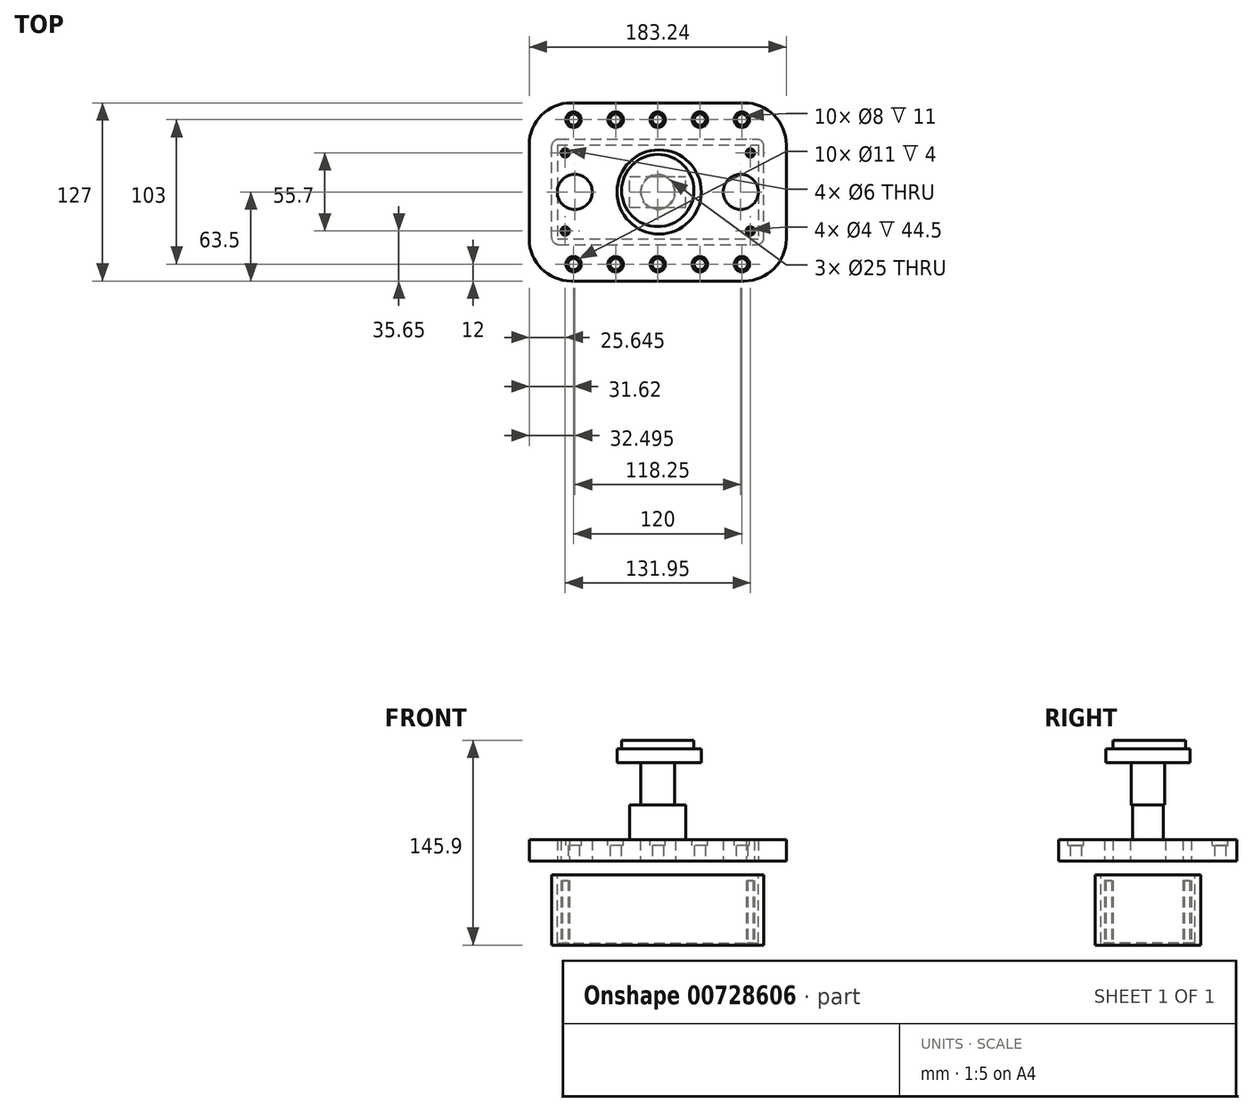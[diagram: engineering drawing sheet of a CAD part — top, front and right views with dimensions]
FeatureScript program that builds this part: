
annotation { "Feature Type Name" : "Feature", "Feature Type Description" : "" }
export const myFeature = defineFeature(function(context is Context, id is Id, definition is map)
    precondition{}
    {
        {
            var Q0;
            Q0=qCreatedBy(makeId("Top.planeOp"),FACE);
            var sketch = newSketch(context, id + "F0", { "sketchPlane" : qUnion([Q0])});
            skCircle(sketch, "E0", {"center": v(0, 1.03) * mm, "radius": 25.75 * mm});
            skSolve(sketch);
        }
        {
            var Q0;
            Q0 = qSketchRegion(id + "F0", true);
            extrude(context, id + "F1", {"entities" : qUnion([Q0]), "depth" : 5.9 * mm, "offsetDistance" : 25 * mm});
        }
        {
            var Q0;
            Q0=makeQuery(id+"F1.opExtrude","CAP_FACE",FACE,{"disambiguationData":[OSD([sQuery(id+"F0.wireOp",EDGE,"E0")])],"isStart":true});
            var sketch = newSketch(context, id + "F2", { "sketchPlane" : qUnion([Q0])});
            skCircle(sketch, "E1", {"center": v(1.03, 0) * mm, "radius": 30 * mm});
            skSolve(sketch);
        }
        {
            var Q0;
            Q0 = qSketchRegion(id + "F2", true);
            extrude(context, id + "F3", {"entities" : qUnion([Q0]), "operationType" : NewBodyOperationType.ADD, "depth" : 10.1 * mm, "offsetDistance" : 25 * mm});
        }
        {
            var Q0;
            Q0=makeQuery(id+"F3.opExtrude","CAP_FACE",FACE,{"disambiguationData":[OSD([sQuery(id+"F2.wireOp",EDGE,"E1")])],"isStart":false});
            var sketch = newSketch(context, id + "F4", { "sketchPlane" : qUnion([Q0])});
            skCircle(sketch, "E2", {"center": v(0, 0) * mm, "radius": 12 * mm});
            skSolve(sketch);
        }
        {
            var Q0;
            Q0 = qSketchRegion(id + "F4", true);
            extrude(context, id + "F5", {"entities" : qUnion([Q0]), "operationType" : NewBodyOperationType.ADD, "depth" : 30 * mm, "offsetDistance" : 25 * mm});
        }
        {
            var Q0;
            Q0=makeQuery(id+"F5.opExtrude","CAP_FACE",FACE,{"disambiguationData":[OSD([sQuery(id+"F4.wireOp",EDGE,"E2")])],"isStart":false});
            var sketch = newSketch(context, id + "F6", { "sketchPlane" : qUnion([Q0])});
            skLineSegment(sketch, "E3.bottom", {"start": v(-20, 11) * mm, "end": v(20, 11) * mm});
            skLineSegment(sketch, "E3.top", {"start": v(-20, -11) * mm, "end": v(20, -11) * mm});
            skLineSegment(sketch, "E3.left", {"start": v(-20, 11) * mm, "end": v(-20, -11) * mm});
            skLineSegment(sketch, "E3.right", {"start": v(20, 11) * mm, "end": v(20, -11) * mm});
            skPoint(sketch, "E3.middle", {"position": v(0, 0) * mm});
            skSolve(sketch);
        }
        {
            var Q0;
            Q0 = qSketchRegion(id + "F6", true);
            extrude(context, id + "F7", {"entities" : qUnion([Q0]), "operationType" : NewBodyOperationType.ADD, "depth" : 25 * mm, "offsetDistance" : 25 * mm});
        }
        {
            var Q0;
            Q0=qCreatedBy(makeId("Top.planeOp"),FACE);
            cPlane(context, id + "F8", {"entities" : qUnion([Q0]), "cplaneType" : CPlaneType.OFFSET, "offset" : 90 * mm, "oppositeDirection" : true, "width" : 150 * mm, "height" : 150 * mm});
        }
        {
            var Q0;
            Q0=qCreatedBy(id+"F8.planeOp",FACE);
            var sketch = newSketch(context, id + "F9", { "sketchPlane" : qUnion([Q0])});
            skLineSegment(sketch, "E4.bottom", {"start": v(-75.62, -37.5) * mm, "end": v(75.62, -37.5) * mm});
            skLineSegment(sketch, "E4.top", {"start": v(-75.62, 37.5) * mm, "end": v(75.62, 37.5) * mm});
            skLineSegment(sketch, "E4.left", {"start": v(-75.62, -37.5) * mm, "end": v(-75.62, 37.5) * mm});
            skLineSegment(sketch, "E4.right", {"start": v(75.62, -37.5) * mm, "end": v(75.62, 37.5) * mm});
            skPoint(sketch, "E4.middle", {"position": v(0, 0) * mm});
            skLineSegment(sketch, "E5.bottom", {"start": v(-71.62, 33.5) * mm, "end": v(71.62, 33.5) * mm});
            skLineSegment(sketch, "E5.top", {"start": v(-71.62, -33.5) * mm, "end": v(71.62, -33.5) * mm});
            skLineSegment(sketch, "E5.left", {"start": v(-71.62, 33.5) * mm, "end": v(-71.62, -33.5) * mm});
            skLineSegment(sketch, "E5.right", {"start": v(71.62, 33.5) * mm, "end": v(71.62, -33.5) * mm});
            skSolve(sketch);
        }
        {
            var Q0;
            Q0 = qSketchRegion(id + "F9", true);
            extrude(context, id + "F10", {"entities" : qUnion([Q0]), "oppositeDirection" : true, "depth" : 48.5 * mm, "offsetDistance" : 25 * mm});
        }
        {
            var Q0;
            Q0=makeQuery(id+"F10.opExtrude","CAP_FACE",FACE,{"disambiguationData":[OSD([sQuery(id+"F9.wireOp",EDGE,"E4.bottom"),sQuery(id+"F9.wireOp",EDGE,"E4.top"),sQuery(id+"F9.wireOp",EDGE,"E4.left"),sQuery(id+"F9.wireOp",EDGE,"E4.right"),sQuery(id+"F9.wireOp",EDGE,"E5.bottom"),sQuery(id+"F9.wireOp",EDGE,"E5.top"),sQuery(id+"F9.wireOp",EDGE,"E5.left"),sQuery(id+"F9.wireOp",EDGE,"E5.right")])],"isStart":false});
            var sketch = newSketch(context, id + "F11", { "sketchPlane" : qUnion([Q0])});
            skLineSegment(sketch, "E6.bottom", {"start": v(-75.62, 37.5) * mm, "end": v(75.62, 37.5) * mm});
            skLineSegment(sketch, "E6.top", {"start": v(-75.62, -37.5) * mm, "end": v(75.62, -37.5) * mm});
            skLineSegment(sketch, "E6.left", {"start": v(-75.62, 37.5) * mm, "end": v(-75.62, -37.5) * mm});
            skLineSegment(sketch, "E6.right", {"start": v(75.62, 37.5) * mm, "end": v(75.62, -37.5) * mm});
            skSolve(sketch);
        }
        {
            var Q0;
            Q0 = qSketchRegion(id + "F11", true);
            extrude(context, id + "F12", {"entities" : qUnion([Q0]), "operationType" : NewBodyOperationType.ADD, "depth" : 1.5 * mm, "offsetDistance" : 25 * mm});
        }
        {
            var Q0;
            Q0=makeQuery(id+"F12.opExtrude","CAP_FACE",FACE,{"disambiguationData":[OSD([sQuery(id+"F11.wireOp",EDGE,"E6.bottom"),sQuery(id+"F11.wireOp",EDGE,"E6.top"),sQuery(id+"F11.wireOp",EDGE,"E6.left"),sQuery(id+"F11.wireOp",EDGE,"E6.right")])],"isStart":true});
            var sketch = newSketch(context, id + "F13", { "sketchPlane" : qUnion([Q0])});
            skCircle(sketch, "E7", {"center": v(65.97, 27.85) * mm, "radius": 3 * mm});
            skLineSegment(sketch, "E8", {"start": v(62.97, 33.5) * mm, "end": v(62.97, -33.5) * mm, "construction": true});
            skLineSegment(sketch, "E9", {"start": v(71.62, 24.85) * mm, "end": v(-71.62, 24.85) * mm, "construction": true});
            skCircle(sketch, "E10", {"center": v(65.97, 27.85) * mm, "radius": 2 * mm});
            skLineSegment(sketch, "E11", {"start": v(0, 33.5) * mm, "end": v(0, -33.5) * mm, "construction": true});
            skLineSegment(sketch, "E12", {"start": v(71.62, 0) * mm, "end": v(-71.62, 0) * mm, "construction": true});
            skCircle(sketch, "E13.MirrorC", {"center": v(-65.97, 27.85) * mm, "radius": 2 * mm});
            skCircle(sketch, "E14.MirrorC", {"center": v(-65.97, 27.85) * mm, "radius": 3 * mm});
            skCircle(sketch, "E15.MirrorC", {"center": v(65.97, -27.85) * mm, "radius": 2 * mm});
            skCircle(sketch, "E16.MirrorC", {"center": v(65.97, -27.85) * mm, "radius": 3 * mm});
            skCircle(sketch, "E17.MirrorC", {"center": v(-65.97, -27.85) * mm, "radius": 2 * mm});
            skCircle(sketch, "E18.MirrorC", {"center": v(-65.97, -27.85) * mm, "radius": 3 * mm});
            skSolve(sketch);
        }
        {
            var Q0;
            Q0 = qSketchRegion(id + "F13", true);
            extrude(context, id + "F14", {"entities" : qUnion([Q0]), "operationType" : NewBodyOperationType.ADD, "depth" : 44.5 * mm, "offsetDistance" : 25 * mm});
        }
        {
            var Q0;
            Q0=makeQuery(id+"F12.boolean.opBoolean","MERGE",EDGE,{"derivedFrom":[makeQuery(id+"F10.opExtrude","SWEPT_EDGE",EDGE,{"disambiguationData":[OSD([sQuery(id+"F9.wireOp",EDGE,"E4.top"),sQuery(id+"F9.wireOp",EDGE,"E4.left")])]}),makeQuery(id+"F12.opExtrude","SWEPT_EDGE",EDGE,{"disambiguationData":[OSD([sQuery(id+"F11.wireOp",EDGE,"E6.top"),sQuery(id+"F11.wireOp",EDGE,"E6.left")])]})]});
            var Q1;
            Q1=makeQuery(id+"F12.boolean.opBoolean","MERGE",EDGE,{"derivedFrom":[makeQuery(id+"F10.opExtrude","SWEPT_EDGE",EDGE,{"disambiguationData":[OSD([sQuery(id+"F9.wireOp",EDGE,"E4.bottom"),sQuery(id+"F9.wireOp",EDGE,"E4.left")])]}),makeQuery(id+"F12.opExtrude","SWEPT_EDGE",EDGE,{"disambiguationData":[OSD([sQuery(id+"F11.wireOp",EDGE,"E6.bottom"),sQuery(id+"F11.wireOp",EDGE,"E6.left")])]})]});
            var Q2;
            Q2=makeQuery(id+"F12.boolean.opBoolean","MERGE",EDGE,{"derivedFrom":[makeQuery(id+"F10.opExtrude","SWEPT_EDGE",EDGE,{"disambiguationData":[OSD([sQuery(id+"F9.wireOp",EDGE,"E4.bottom"),sQuery(id+"F9.wireOp",EDGE,"E4.right")])]}),makeQuery(id+"F12.opExtrude","SWEPT_EDGE",EDGE,{"disambiguationData":[OSD([sQuery(id+"F11.wireOp",EDGE,"E6.bottom"),sQuery(id+"F11.wireOp",EDGE,"E6.right")])]})]});
            var Q3;
            Q3=makeQuery(id+"F12.boolean.opBoolean","MERGE",EDGE,{"derivedFrom":[makeQuery(id+"F10.opExtrude","SWEPT_EDGE",EDGE,{"disambiguationData":[OSD([sQuery(id+"F9.wireOp",EDGE,"E4.top"),sQuery(id+"F9.wireOp",EDGE,"E4.right")])]}),makeQuery(id+"F12.opExtrude","SWEPT_EDGE",EDGE,{"disambiguationData":[OSD([sQuery(id+"F11.wireOp",EDGE,"E6.top"),sQuery(id+"F11.wireOp",EDGE,"E6.right")])]})]});
            fillet(context, id + "F15", {"entities" : qUnion([Q0, Q1, Q2, Q3]), "radius" : 5 * mm, "tangentPropagation" : true, "allowEdgeOverflow" : false});
        }
        {
            var Q0;
            Q0=qCreatedBy(id+"F8.planeOp",FACE);
            cPlane(context, id + "F16", {"entities" : qUnion([Q0]), "cplaneType" : CPlaneType.OFFSET, "offset" : 10 * mm, "width" : 150 * mm, "height" : 150 * mm});
        }
        {
            var Q0;
            Q0=qCreatedBy(id+"F16.planeOp",FACE);
            var sketch = newSketch(context, id + "F17", { "sketchPlane" : qUnion([Q0])});
            skLineSegment(sketch, "E19.0", {"start": v(-71.62, -33.5) * mm, "end": v(71.62, -33.5) * mm, "construction": true});
            skLineSegment(sketch, "E19.1", {"start": v(71.62, 33.5) * mm, "end": v(71.62, -33.5) * mm, "construction": true});
            skLineSegment(sketch, "E19.2", {"start": v(-71.62, 33.5) * mm, "end": v(71.62, 33.5) * mm, "construction": true});
            skLineSegment(sketch, "E19.3", {"start": v(-71.62, 33.5) * mm, "end": v(-71.62, -33.5) * mm, "construction": true});
            skLineSegment(sketch, "E20", {"start": v(71.62, 0) * mm, "end": v(-71.62, 0) * mm, "construction": true});
            skCircle(sketch, "E21", {"center": v(59.12, 0) * mm, "radius": 12.5 * mm});
            skCircle(sketch, "E22", {"center": v(59.12, 0) * mm, "radius": 30 * mm, "construction": true});
            skCircle(sketch, "E23", {"center": v(-59.12, 0) * mm, "radius": 12.5 * mm});
            skLineSegment(sketch, "E24", {"start": v(0, 33.5) * mm, "end": v(0, -33.5) * mm, "construction": true});
            skCircle(sketch, "E25", {"center": v(0, 0) * mm, "radius": 12.5 * mm});
            skCircle(sketch, "E26", {"center": v(0, 0) * mm, "radius": 30 * mm, "construction": true});
            skCircle(sketch, "E27", {"center": v(-59.12, 0) * mm, "radius": 30 * mm, "construction": true});
            skLineSegment(sketch, "E28.bottom", {"start": v(-91.62, 63.5) * mm, "end": v(91.62, 63.5) * mm});
            skLineSegment(sketch, "E28.top", {"start": v(-91.62, -63.5) * mm, "end": v(91.63, -63.5) * mm});
            skLineSegment(sketch, "E28.left", {"start": v(-91.62, 63.5) * mm, "end": v(-91.62, -63.5) * mm});
            skLineSegment(sketch, "E28.right", {"start": v(91.62, 63.5) * mm, "end": v(91.62, -63.5) * mm});
            skCircle(sketch, "E29.0", {"center": v(-65.97, -27.85) * mm, "radius": 3 * mm});
            skCircle(sketch, "E29.1", {"center": v(65.97, -27.85) * mm, "radius": 3 * mm});
            skCircle(sketch, "E29.2", {"center": v(65.97, 27.85) * mm, "radius": 3 * mm});
            skCircle(sketch, "E29.3", {"center": v(-65.97, 27.85) * mm, "radius": 3 * mm});
            skLineSegment(sketch, "E30", {"start": v(0, -33.5) * mm, "end": v(0, -63.5) * mm, "construction": true});
            skCircle(sketch, "E31", {"center": v(0, -51.5) * mm, "radius": 4 * mm});
            skCircle(sketch, "E32.1.0.0", {"center": v(30, -51.5) * mm, "radius": 4 * mm});
            skCircle(sketch, "E32.2.0.0", {"center": v(60, -51.5) * mm, "radius": 4 * mm});
            skLineSegment(sketch, "E32.direction1", {"start": v(0, -51.5) * mm, "end": v(30, -51.5) * mm, "construction": true});
            skCircle(sketch, "E33.MirrorC", {"center": v(-60, -51.5) * mm, "radius": 4 * mm});
            skCircle(sketch, "E34.MirrorC", {"center": v(-30, -51.5) * mm, "radius": 4 * mm});
            skCircle(sketch, "E35.MirrorC", {"center": v(60, 51.5) * mm, "radius": 4 * mm});
            skCircle(sketch, "E36.MirrorC", {"center": v(30, 51.5) * mm, "radius": 4 * mm});
            skCircle(sketch, "E37.MirrorC", {"center": v(0, 51.5) * mm, "radius": 4 * mm});
            skCircle(sketch, "E38.MirrorC", {"center": v(-30, 51.5) * mm, "radius": 4 * mm});
            skCircle(sketch, "E39.MirrorC", {"center": v(-60, 51.5) * mm, "radius": 4 * mm});
            skSolve(sketch);
        }
        {
            var Q0;
            Q0 = qSketchRegion(id + "F17", true);
            extrude(context, id + "F18", {"entities" : qUnion([Q0]), "depth" : 15 * mm, "offsetDistance" : 25 * mm});
        }
        {
            var Q0;
            Q0=makeQuery(id+"F18.opExtrude","SWEPT_EDGE",EDGE,{"disambiguationData":[OSD([sQuery(id+"F17.wireOp",EDGE,"E28.bottom"),sQuery(id+"F17.wireOp",EDGE,"E28.right")])]});
            var Q1;
            Q1=makeQuery(id+"F18.opExtrude","SWEPT_EDGE",EDGE,{"disambiguationData":[OSD([sQuery(id+"F17.wireOp",EDGE,"E28.top"),sQuery(id+"F17.wireOp",EDGE,"E28.right")])]});
            var Q2;
            Q2=makeQuery(id+"F18.opExtrude","SWEPT_EDGE",EDGE,{"disambiguationData":[OSD([sQuery(id+"F17.wireOp",EDGE,"E28.top"),sQuery(id+"F17.wireOp",EDGE,"E28.left")])]});
            var Q3;
            Q3=makeQuery(id+"F18.opExtrude","SWEPT_EDGE",EDGE,{"disambiguationData":[OSD([sQuery(id+"F17.wireOp",EDGE,"E28.bottom"),sQuery(id+"F17.wireOp",EDGE,"E28.left")])]});
            fillet(context, id + "F19", {"entities" : qUnion([Q0, Q1, Q2, Q3]), "radius" : 30 * mm, "tangentPropagation" : true, "allowEdgeOverflow" : false});
        }
        {
            var Q0;
            Q0=makeQuery(id+"F18.opExtrude","CAP_FACE",FACE,{"disambiguationData":[OSD([sQuery(id+"F17.wireOp",EDGE,"E21"),sQuery(id+"F17.wireOp",EDGE,"E23"),sQuery(id+"F17.wireOp",EDGE,"E25"),sQuery(id+"F17.wireOp",EDGE,"E28.bottom"),sQuery(id+"F17.wireOp",EDGE,"E28.top"),sQuery(id+"F17.wireOp",EDGE,"E28.left"),sQuery(id+"F17.wireOp",EDGE,"E28.right"),sQuery(id+"F17.wireOp",EDGE,"E29.0"),sQuery(id+"F17.wireOp",EDGE,"E29.1"),sQuery(id+"F17.wireOp",EDGE,"E29.2"),sQuery(id+"F17.wireOp",EDGE,"E29.3"),sQuery(id+"F17.wireOp",EDGE,"E31"),sQuery(id+"F17.wireOp",EDGE,"E32.1.0.0"),sQuery(id+"F17.wireOp",EDGE,"E32.2.0.0"),sQuery(id+"F17.wireOp",EDGE,"E33.MirrorC"),sQuery(id+"F17.wireOp",EDGE,"E34.MirrorC"),sQuery(id+"F17.wireOp",EDGE,"E35.MirrorC"),sQuery(id+"F17.wireOp",EDGE,"E36.MirrorC"),sQuery(id+"F17.wireOp",EDGE,"E37.MirrorC"),sQuery(id+"F17.wireOp",EDGE,"E38.MirrorC"),sQuery(id+"F17.wireOp",EDGE,"E39.MirrorC")])],"isStart":false});
            var sketch = newSketch(context, id + "F20", { "sketchPlane" : qUnion([Q0])});
            skCircle(sketch, "E40", {"center": v(-60, 51.5) * mm, "radius": 5.5 * mm});
            skCircle(sketch, "E41", {"center": v(-30, 51.5) * mm, "radius": 5.5 * mm});
            skCircle(sketch, "E42", {"center": v(0, 51.5) * mm, "radius": 5.5 * mm});
            skCircle(sketch, "E43", {"center": v(30, 51.5) * mm, "radius": 5.5 * mm});
            skCircle(sketch, "E44", {"center": v(60, 51.5) * mm, "radius": 5.5 * mm});
            skCircle(sketch, "E45", {"center": v(60, -51.5) * mm, "radius": 5.5 * mm});
            skCircle(sketch, "E46", {"center": v(30, -51.5) * mm, "radius": 5.5 * mm});
            skCircle(sketch, "E47", {"center": v(0, -51.5) * mm, "radius": 5.5 * mm});
            skCircle(sketch, "E48", {"center": v(-30, -51.5) * mm, "radius": 5.5 * mm});
            skCircle(sketch, "E49", {"center": v(-60, -51.5) * mm, "radius": 5.5 * mm});
            skSolve(sketch);
        }
        {
            var Q0;
            Q0 = qSketchRegion(id + "F20", true);
            extrude(context, id + "F21", {"entities" : qUnion([Q0]), "operationType" : NewBodyOperationType.REMOVE, "oppositeDirection" : true, "depth" : 4 * mm, "offsetDistance" : 25 * mm});
        }
    });
